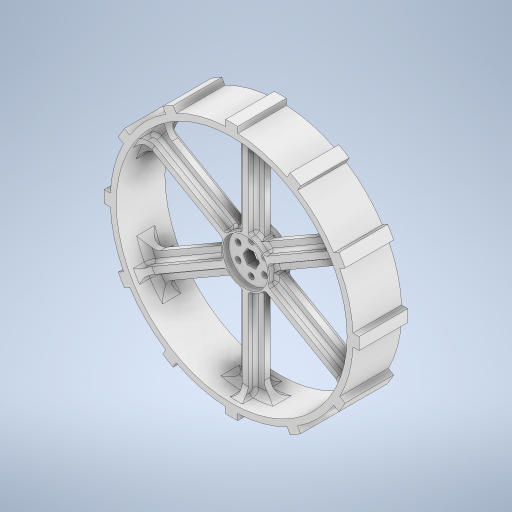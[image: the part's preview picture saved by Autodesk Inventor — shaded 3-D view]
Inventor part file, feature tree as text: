
AUTODESK INVENTOR PART (.ipt)
format: ipt  version: 2023 (Build 270158000, 158)  size: 903,680 bytes
history: native  units: in
note: dims shown in document units (in); Inventor stores cm internally (conversion verified against a paired STEP export)
features: fillet x5, sketch x5, extrude x4, pattern_circular x2
ambient origin geometry x8: Origin, YZ Plane, XZ Plane, XY Plane, X Axis, Y Axis, Z Axis, Center Point
bodies: Solid1 (feature_tree)
feature tree (16):
  extrude  "Extrusion1"  Depth=0.25in
  extrude  "Extrusion2"  Depth=2.0in
  extrude  "Extrusion3"  Depth=0.375in TaperAngle=0.0deg
  extrude  "Extrusion4"  Depth=0.25in
  fillet  "Fillet2"  Radius=0.875in
  fillet  "Fillet3"  Radius=0.25in
  fillet  "Fillet4"  Radius=0.875in
  fillet  "Fillet1"  Radius=0.9375in
  fillet  "Fillet5"  Radius=0.25in
  pattern_circular  "Circular Pattern1"  [2 undecoded]
  pattern_circular  "Circular Pattern5"  [2 undecoded]
  sketch  "Sketch1"  dims[d0=10.0in d2=0.25in]
  sketch  "Sketch2"  dims[d3=2.0in d4=0.0in d5=2.0in]
  sketch  "Sketch3"  dims[d6=0.5787in d7=0.375in d8=0.0in]
  sketch  "Sketch5"  dims[d9=2.0in d10=0.0625in d11=0.875in d12=0.0in d15=0.25in d16=0.875in d17=0.9375in d18=0.25in]
  sketch  "Sketch9"  dims[d20=0.875in d21=0.0in d22=0.125in d23=0.5in d24=0.375in d25=0.25in d26=0.125in d27=2.3622in d28=360.0deg d30=0.2362in d31=0.625in d32=2.3622in d34=360.0deg d56=0.0in d57=0.5in d58=2.0in d59=0.25in d60=0.0in d61=4.7244in d62=360.0deg]
note: 4 required parameter values undecoded (feature->parameter linkage not recoverable at this tier; creation-order binding heuristic only, values carry confidence <= 0.55)
